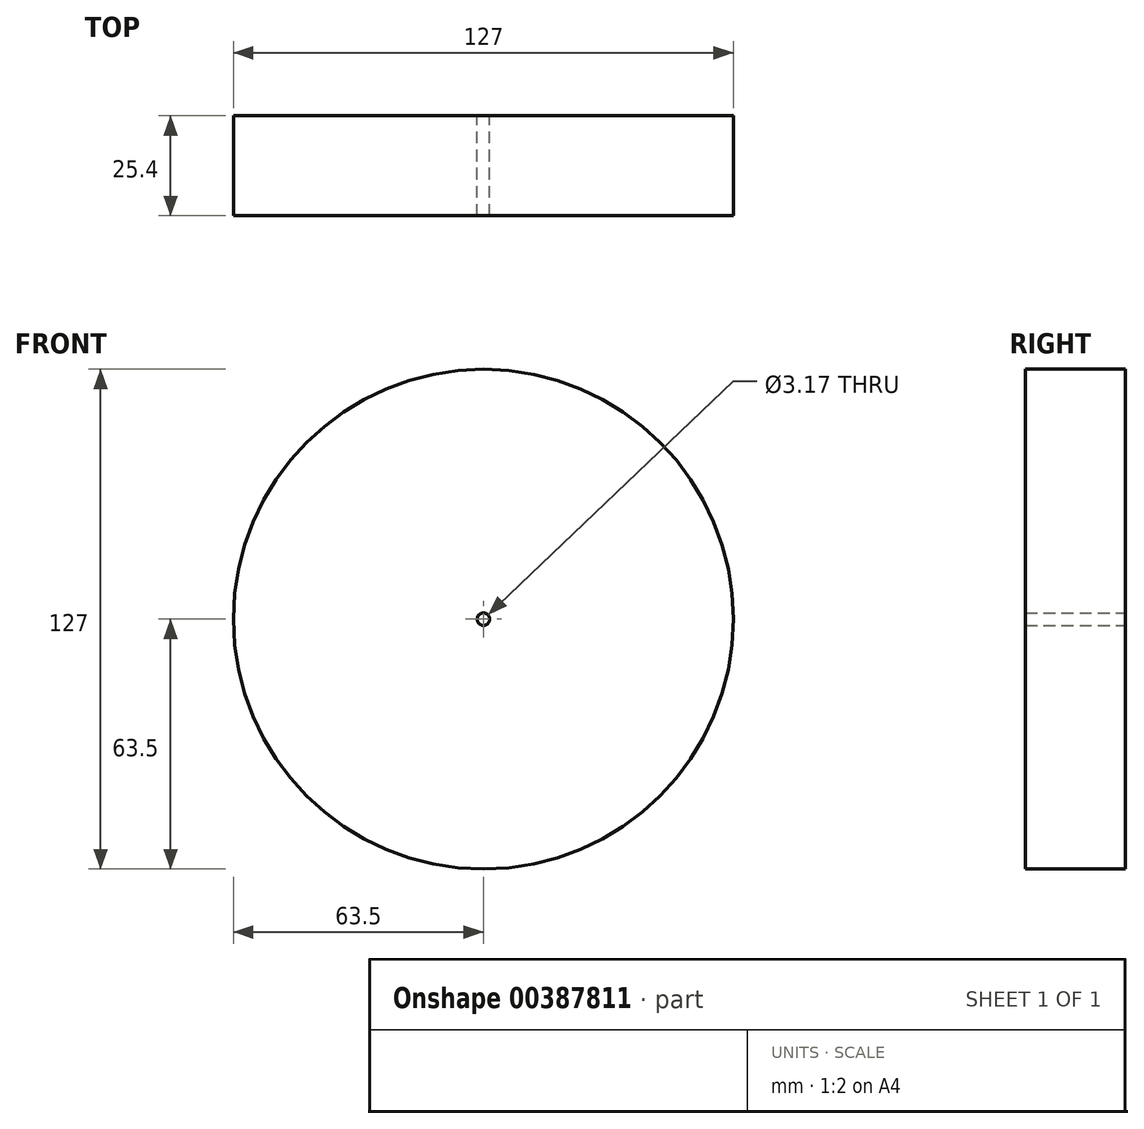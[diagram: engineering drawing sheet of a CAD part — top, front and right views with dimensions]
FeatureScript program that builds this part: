
annotation { "Feature Type Name" : "Feature", "Feature Type Description" : "" }
export const myFeature = defineFeature(function(context is Context, id is Id, definition is map)
    precondition{}
    {
        {
            var Q0;
            Q0=qCreatedBy(makeId("Front.planeOp"),FACE);
            var sketch = newSketch(context, id + "F0", { "sketchPlane" : qUnion([Q0])});
            skCircle(sketch, "E0", {"center": v(0, 0) * mm, "radius": 63.5 * mm});
            skCircle(sketch, "E1", {"center": v(0, 0) * mm, "radius": 1.59 * mm});
            skSolve(sketch);
        }
        {
            var Q0;
            Q0=makeQuery(id+"F0.imprint","IMPRINT",FACE,{"disambiguationData":[TD([[makeQuery(id+"F0.imprint","IMPRINT",EDGE,{"derivedFrom":sQuery(id+"F0.wireOp",EDGE,"E0")}),1.0]])]});
            extrude(context, id + "F1", {"entities" : qUnion([Q0]), "depth" : 25.4 * mm, "offsetDistance" : 25.4 * mm});
        }
    });
